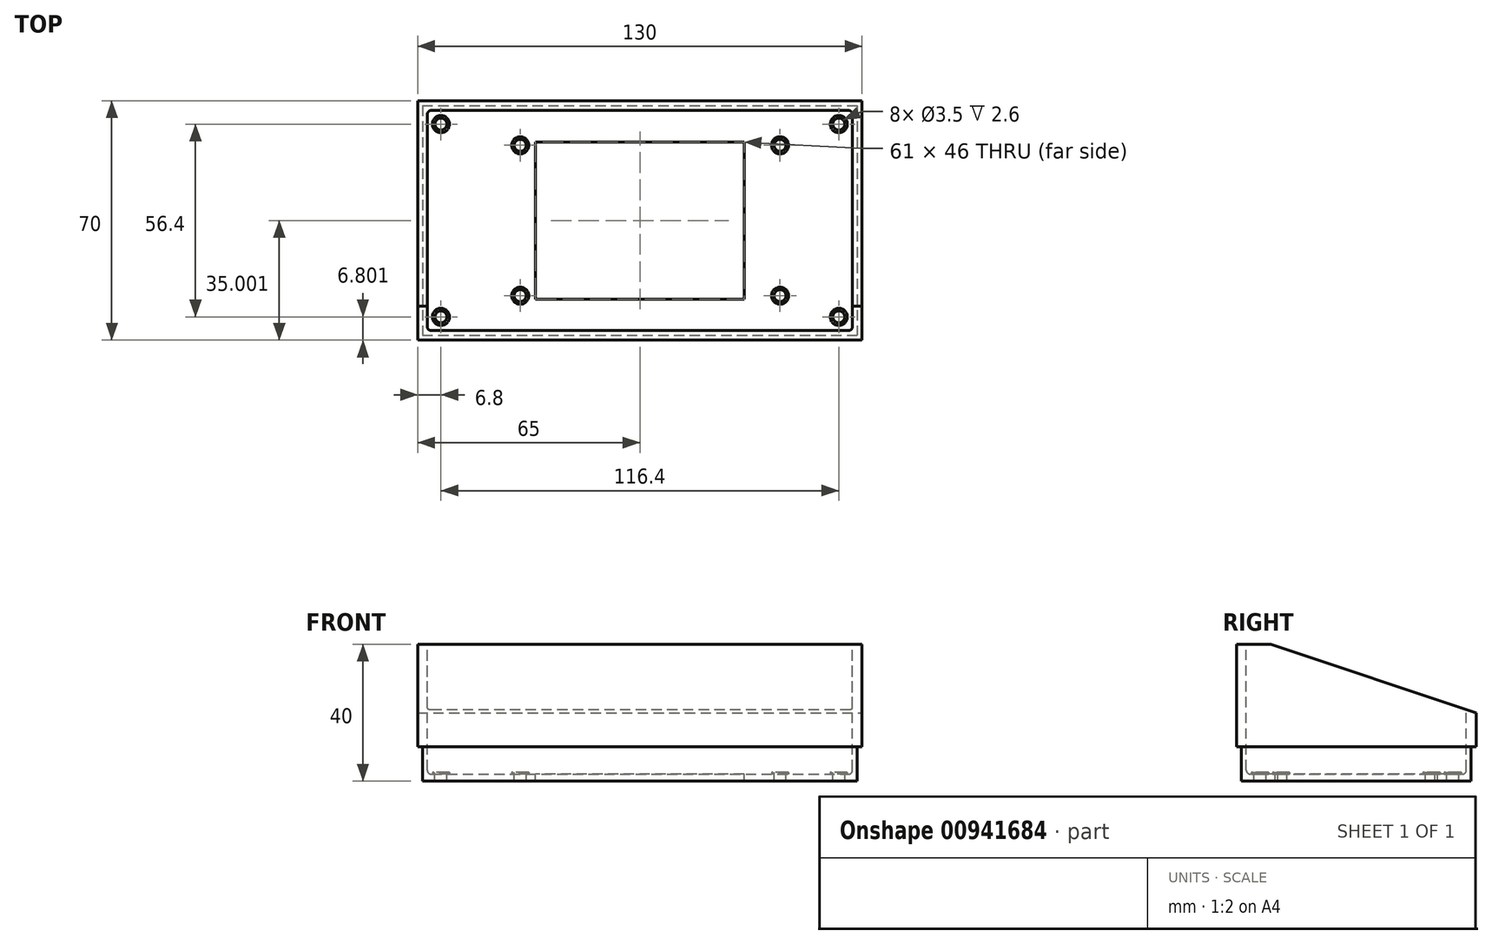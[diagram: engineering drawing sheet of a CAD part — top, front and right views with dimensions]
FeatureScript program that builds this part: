
annotation { "Feature Type Name" : "Feature", "Feature Type Description" : "" }
export const myFeature = defineFeature(function(context is Context, id is Id, definition is map)
    precondition{}
    {
        {
            var Q0;
            Q0=qCreatedBy(makeId("Top.planeOp"),FACE);
            var sketch = newSketch(context, id + "F0", { "sketchPlane" : qUnion([Q0])});
            skLineSegment(sketch, "E0.bottom", {"start": v(-87.5, 48.26) * mm, "end": v(42.5, 48.26) * mm});
            skLineSegment(sketch, "E0.top", {"start": v(-87.5, -21.74) * mm, "end": v(42.5, -21.74) * mm});
            skLineSegment(sketch, "E0.left", {"start": v(-87.5, 48.26) * mm, "end": v(-87.5, -21.74) * mm});
            skLineSegment(sketch, "E0.right", {"start": v(42.5, 48.26) * mm, "end": v(42.5, -21.74) * mm});
            skSolve(sketch);
        }
        {
            var Q0;
            Q0=makeQuery(id+"F0.imprint","IMPRINT",FACE,{"disambiguationData":[TD([[makeQuery(id+"F0.imprint","IMPRINT",EDGE,{"derivedFrom":sQuery(id+"F0.wireOp",EDGE,"E0.bottom")}),-1.0]])]});
            extrude(context, id + "F1", {"entities" : qUnion([Q0]), "depth" : 40 * mm, "offsetDistance" : 25 * mm});
        }
        {
            var Q0;
            Q0=makeQuery(id+"F1.opExtrude","CAP_FACE",FACE,{"disambiguationData":[OSD([sQuery(id+"F0.wireOp",EDGE,"E0.bottom"),sQuery(id+"F0.wireOp",EDGE,"E0.top"),sQuery(id+"F0.wireOp",EDGE,"E0.left"),sQuery(id+"F0.wireOp",EDGE,"E0.right")])],"isStart":false});
            var sketch = newSketch(context, id + "F2", { "sketchPlane" : qUnion([Q0])});
            skLineSegment(sketch, "E1.0", {"start": v(39.7, 45.46) * mm, "end": v(39.7, -18.94) * mm});
            skLineSegment(sketch, "E1.1", {"start": v(-84.7, 45.46) * mm, "end": v(39.7, 45.46) * mm});
            skLineSegment(sketch, "E1.2", {"start": v(-84.7, 45.46) * mm, "end": v(-84.7, -18.94) * mm});
            skLineSegment(sketch, "E1.3", {"start": v(-84.7, -18.94) * mm, "end": v(39.7, -18.94) * mm});
            skSolve(sketch);
        }
        {
            var Q0;
            Q0=makeQuery(id+"F2.imprint","IMPRINT",FACE,{"disambiguationData":[TD([[makeQuery(id+"F2.imprint","IMPRINT",EDGE,{"derivedFrom":sQuery(id+"F2.wireOp",EDGE,"E1.0")}),-1.0]])]});
            extrude(context, id + "F3", {"entities" : qUnion([Q0]), "operationType" : NewBodyOperationType.REMOVE, "oppositeDirection" : true, "depth" : 38 * mm, "offsetDistance" : 25 * mm});
        }
        {
            var Q0;
            Q0=makeQuery(id+"F1.opExtrude","SWEPT_FACE",FACE,{"disambiguationData":[OSD([sQuery(id+"F0.wireOp",EDGE,"E0.right")])]});
            var sketch = newSketch(context, id + "F4", { "sketchPlane" : qUnion([Q0])});
            skLineSegment(sketch, "E2", {"start": v(-11.74, 40) * mm, "end": v(48.26, 20) * mm});
            skLineSegment(sketch, "E3", {"start": v(48.26, 20) * mm, "end": v(48.26, 40) * mm});
            skLineSegment(sketch, "E4", {"start": v(48.26, 40) * mm, "end": v(-11.74, 40) * mm});
            skSolve(sketch);
        }
        {
            var Q0;
            Q0=makeQuery(id+"F4.imprint","IMPRINT",FACE,{"disambiguationData":[TD([[makeQuery(id+"F4.imprint","IMPRINT",EDGE,{"derivedFrom":sQuery(id+"F4.wireOp",EDGE,"E2")}),1.0]])]});
            extrude(context, id + "F5", {"entities" : qUnion([Q0]), "operationType" : NewBodyOperationType.REMOVE, "oppositeDirection" : true, "depth" : 146.2 * mm, "offsetDistance" : 25 * mm});
        }
        {
            var Q0;
            Q0=makeQuery(id+"F1.opExtrude","CAP_FACE",FACE,{"disambiguationData":[OSD([sQuery(id+"F0.wireOp",EDGE,"E0.bottom"),sQuery(id+"F0.wireOp",EDGE,"E0.top"),sQuery(id+"F0.wireOp",EDGE,"E0.left"),sQuery(id+"F0.wireOp",EDGE,"E0.right")])],"isStart":true});
            var sketch = newSketch(context, id + "F6", { "sketchPlane" : qUnion([Q0])});
            skLineSegment(sketch, "E5.0", {"start": v(-86.1, -46.86) * mm, "end": v(41.1, -46.86) * mm});
            skLineSegment(sketch, "E5.1", {"start": v(-86.1, -46.86) * mm, "end": v(-86.1, 20.34) * mm});
            skLineSegment(sketch, "E5.2", {"start": v(-86.1, 20.34) * mm, "end": v(41.1, 20.34) * mm});
            skLineSegment(sketch, "E5.3", {"start": v(41.1, -46.86) * mm, "end": v(41.1, 20.34) * mm});
            skLineSegment(sketch, "E6.bottom", {"start": v(42.5, -48.26) * mm, "end": v(-87.5, -48.26) * mm});
            skLineSegment(sketch, "E6.top", {"start": v(42.5, 21.74) * mm, "end": v(-87.5, 21.74) * mm});
            skLineSegment(sketch, "E6.left", {"start": v(42.5, -48.26) * mm, "end": v(42.5, 21.74) * mm});
            skLineSegment(sketch, "E6.right", {"start": v(-87.5, -48.26) * mm, "end": v(-87.5, 21.74) * mm});
            skSolve(sketch);
        }
        {
            var Q0;
            Q0=makeQuery(id+"F6.imprint","IMPRINT",FACE,{"disambiguationData":[TD([[makeQuery(id+"F6.imprint","IMPRINT",EDGE,{"derivedFrom":sQuery(id+"F6.wireOp",EDGE,"E5.0")}),-1.0]])]});
            extrude(context, id + "F7", {"entities" : qUnion([Q0]), "operationType" : NewBodyOperationType.REMOVE, "oppositeDirection" : true, "depth" : 10 * mm, "offsetDistance" : 25 * mm});
        }
        {
            var Q0;
            Q0=makeQuery(id+"F3.boolean.opBoolean","COPY",FACE,{"derivedFrom":makeQuery(id+"F3.opExtrude","CAP_FACE",FACE,{"disambiguationData":[OSD([sQuery(id+"F2.wireOp",EDGE,"E1.0"),sQuery(id+"F2.wireOp",EDGE,"E1.1"),sQuery(id+"F2.wireOp",EDGE,"E1.2"),sQuery(id+"F2.wireOp",EDGE,"E1.3")])],"isStart":false})});
            var sketch = newSketch(context, id + "F8", { "sketchPlane" : qUnion([Q0])});
            skLineSegment(sketch, "E7.bottom", {"start": v(8, -9.74) * mm, "end": v(-53, -9.74) * mm});
            skLineSegment(sketch, "E7.top", {"start": v(8, 36.26) * mm, "end": v(-53, 36.26) * mm});
            skLineSegment(sketch, "E7.left", {"start": v(8, -9.74) * mm, "end": v(8, 36.26) * mm});
            skLineSegment(sketch, "E7.right", {"start": v(-53, -9.74) * mm, "end": v(-53, 36.26) * mm});
            skLineSegment(sketch, "E8.0", {"start": v(-57.5, -9.74) * mm, "end": v(-57.5, 36.26) * mm, "construction": true});
            skLineSegment(sketch, "E9.0", {"start": v(18.5, -9.74) * mm, "end": v(18.5, 36.26) * mm, "construction": true});
            skLineSegment(sketch, "E10.0", {"start": v(18.5, -8.74) * mm, "end": v(-57.5, -8.74) * mm, "construction": true});
            skLineSegment(sketch, "E11.0", {"start": v(18.5, 35.26) * mm, "end": v(-57.5, 35.26) * mm, "construction": true});
            skCircle(sketch, "E12", {"center": v(18.5, -8.74) * mm, "radius": 1.75 * mm});
            skCircle(sketch, "E13", {"center": v(18.5, 35.26) * mm, "radius": 1.75 * mm});
            skCircle(sketch, "E14", {"center": v(-57.5, -8.74) * mm, "radius": 1.75 * mm});
            skCircle(sketch, "E15", {"center": v(-57.5, 35.26) * mm, "radius": 1.75 * mm});
            skSolve(sketch);
        }
        {
            var Q0;
            Q0=makeQuery(id+"F8.imprint","IMPRINT",FACE,{"disambiguationData":[TD([[makeQuery(id+"F8.imprint","IMPRINT",EDGE,{"derivedFrom":sQuery(id+"F8.wireOp",EDGE,"E7.bottom")}),-1.0]])]});
            var Q1;
            Q1=makeQuery(id+"F8.imprint","IMPRINT",FACE,{"disambiguationData":[TD([[makeQuery(id+"F8.imprint","IMPRINT",EDGE,{"derivedFrom":sQuery(id+"F8.wireOp",EDGE,"E15")}),1.0]])]});
            var Q2;
            Q2=makeQuery(id+"F8.imprint","IMPRINT",FACE,{"disambiguationData":[TD([[makeQuery(id+"F8.imprint","IMPRINT",EDGE,{"derivedFrom":sQuery(id+"F8.wireOp",EDGE,"E13")}),1.0]])]});
            var Q3;
            Q3=makeQuery(id+"F8.imprint","IMPRINT",FACE,{"disambiguationData":[TD([[makeQuery(id+"F8.imprint","IMPRINT",EDGE,{"derivedFrom":sQuery(id+"F8.wireOp",EDGE,"E12")}),1.0]])]});
            var Q4;
            Q4=makeQuery(id+"F8.imprint","IMPRINT",FACE,{"disambiguationData":[TD([[makeQuery(id+"F8.imprint","IMPRINT",EDGE,{"derivedFrom":sQuery(id+"F8.wireOp",EDGE,"E14")}),1.0]])]});
            extrude(context, id + "F9", {"entities" : qUnion([Q0, Q1, Q2, Q3, Q4]), "operationType" : NewBodyOperationType.REMOVE, "oppositeDirection" : true, "depth" : 25 * mm, "offsetDistance" : 25 * mm, "hasSecondDirection" : true, "secondDirectionOppositeDirection" : false, "secondDirectionDepth" : 25 * mm});
        }
        {
            var Q0;
            Q0=makeQuery(id+"F3.boolean.opBoolean","COPY",FACE,{"derivedFrom":makeQuery(id+"F3.opExtrude","CAP_FACE",FACE,{"disambiguationData":[OSD([sQuery(id+"F2.wireOp",EDGE,"E1.0"),sQuery(id+"F2.wireOp",EDGE,"E1.1"),sQuery(id+"F2.wireOp",EDGE,"E1.2"),sQuery(id+"F2.wireOp",EDGE,"E1.3")])],"isStart":false})});
            var sketch = newSketch(context, id + "F10", { "sketchPlane" : qUnion([Q0])});
            skCircle(sketch, "E16", {"center": v(-80.7, 41.46) * mm, "radius": 1.75 * mm});
            skCircle(sketch, "E17", {"center": v(-80.7, -14.94) * mm, "radius": 1.75 * mm});
            skCircle(sketch, "E18", {"center": v(35.7, -14.94) * mm, "radius": 1.75 * mm});
            skCircle(sketch, "E19", {"center": v(35.7, 41.46) * mm, "radius": 1.75 * mm});
            skSolve(sketch);
        }
        {
            var Q0;
            Q0=makeQuery(id+"F10.imprint","IMPRINT",FACE,{"disambiguationData":[TD([[makeQuery(id+"F10.imprint","IMPRINT",EDGE,{"derivedFrom":sQuery(id+"F10.wireOp",EDGE,"E16")}),1.0]])]});
            var Q1;
            Q1=makeQuery(id+"F10.imprint","IMPRINT",FACE,{"disambiguationData":[TD([[makeQuery(id+"F10.imprint","IMPRINT",EDGE,{"derivedFrom":sQuery(id+"F10.wireOp",EDGE,"E19")}),1.0]])]});
            var Q2;
            Q2=makeQuery(id+"F10.imprint","IMPRINT",FACE,{"disambiguationData":[TD([[makeQuery(id+"F10.imprint","IMPRINT",EDGE,{"derivedFrom":sQuery(id+"F10.wireOp",EDGE,"E18")}),1.0]])]});
            var Q3;
            Q3=makeQuery(id+"F10.imprint","IMPRINT",FACE,{"disambiguationData":[TD([[makeQuery(id+"F10.imprint","IMPRINT",EDGE,{"derivedFrom":sQuery(id+"F10.wireOp",EDGE,"E17")}),1.0]])]});
            extrude(context, id + "F11", {"entities" : qUnion([Q0, Q1, Q2, Q3]), "operationType" : NewBodyOperationType.REMOVE, "oppositeDirection" : true, "depth" : 25 * mm, "offsetDistance" : 25 * mm});
        }
        {
            var Q0;
            Q0=makeQuery(id+"F3.boolean.opBoolean","COPY",FACE,{"derivedFrom":makeQuery(id+"F3.opExtrude","CAP_FACE",FACE,{"disambiguationData":[OSD([sQuery(id+"F2.wireOp",EDGE,"E1.0"),sQuery(id+"F2.wireOp",EDGE,"E1.1"),sQuery(id+"F2.wireOp",EDGE,"E1.2"),sQuery(id+"F2.wireOp",EDGE,"E1.3")])],"isStart":false})});
            var sketch = newSketch(context, id + "F12", { "sketchPlane" : qUnion([Q0])});
            skCircle(sketch, "E20", {"center": v(-57.5, 35.26) * mm, "radius": 2.5 * mm});
            skCircle(sketch, "E21", {"center": v(18.5, 35.26) * mm, "radius": 2.5 * mm});
            skCircle(sketch, "E22", {"center": v(18.5, -8.74) * mm, "radius": 2.5 * mm});
            skCircle(sketch, "E23", {"center": v(-57.5, -8.74) * mm, "radius": 2.5 * mm});
            skCircle(sketch, "E24", {"center": v(-80.7, -14.94) * mm, "radius": 2.5 * mm});
            skCircle(sketch, "E25", {"center": v(-80.7, 41.46) * mm, "radius": 2.5 * mm});
            skCircle(sketch, "E26", {"center": v(35.7, 41.46) * mm, "radius": 2.5 * mm});
            skCircle(sketch, "E27", {"center": v(-80.7, 41.46) * mm, "radius": 1.75 * mm});
            skCircle(sketch, "E28", {"center": v(-57.5, 35.26) * mm, "radius": 1.75 * mm});
            skCircle(sketch, "E29", {"center": v(18.5, 35.26) * mm, "radius": 1.75 * mm});
            skCircle(sketch, "E30", {"center": v(35.7, 41.46) * mm, "radius": 1.75 * mm});
            skCircle(sketch, "E31", {"center": v(18.5, -8.74) * mm, "radius": 1.75 * mm});
            skCircle(sketch, "E32", {"center": v(35.7, -14.94) * mm, "radius": 1.75 * mm});
            skCircle(sketch, "E33", {"center": v(35.7, -14.94) * mm, "radius": 2.5 * mm});
            skCircle(sketch, "E34", {"center": v(-57.5, -8.74) * mm, "radius": 1.75 * mm});
            skCircle(sketch, "E35", {"center": v(-80.7, -14.94) * mm, "radius": 1.75 * mm});
            skSolve(sketch);
        }
        {
            var Q0;
            Q0 = qSketchRegion(id + "F12", true);
            extrude(context, id + "F13", {"entities" : qUnion([Q0]), "operationType" : NewBodyOperationType.ADD, "depth" : .6 * mm, "offsetDistance" : 25 * mm});
        }
        {
            var Q0;
            Q0=makeQuery(id+"F3.boolean.opBoolean","COPY",EDGE,{"derivedFrom":makeQuery(id+"F3.opExtrude","SWEPT_EDGE",EDGE,{"disambiguationData":[OSD([sQuery(id+"F2.wireOp",EDGE,"E1.0"),sQuery(id+"F2.wireOp",EDGE,"E1.1")])]})});
            var Q1;
            Q1=makeQuery(id+"F3.boolean.opBoolean","COPY",EDGE,{"derivedFrom":makeQuery(id+"F3.opExtrude","SWEPT_EDGE",EDGE,{"disambiguationData":[OSD([sQuery(id+"F2.wireOp",EDGE,"E1.1"),sQuery(id+"F2.wireOp",EDGE,"E1.2")])]})});
            var Q2;
            Q2=makeQuery(id+"F3.boolean.opBoolean","COPY",EDGE,{"derivedFrom":makeQuery(id+"F3.opExtrude","SWEPT_EDGE",EDGE,{"disambiguationData":[OSD([sQuery(id+"F2.wireOp",EDGE,"E1.2"),sQuery(id+"F2.wireOp",EDGE,"E1.3")])]})});
            var Q3;
            Q3=makeQuery(id+"F3.boolean.opBoolean","COPY",EDGE,{"derivedFrom":makeQuery(id+"F3.opExtrude","SWEPT_EDGE",EDGE,{"disambiguationData":[OSD([sQuery(id+"F2.wireOp",EDGE,"E1.0"),sQuery(id+"F2.wireOp",EDGE,"E1.3")])]})});
            var Q4;
            Q4=makeQuery(id+"F3.boolean.opBoolean","COPY",EDGE,{"derivedFrom":makeQuery(id+"F3.opExtrude","CAP_EDGE",EDGE,{"disambiguationData":[OSD([sQuery(id+"F2.wireOp",EDGE,"E1.2")])],"isStart":false})});
            var Q5;
            Q5=makeQuery(id+"F3.boolean.opBoolean","COPY",EDGE,{"derivedFrom":makeQuery(id+"F3.opExtrude","CAP_EDGE",EDGE,{"disambiguationData":[OSD([sQuery(id+"F2.wireOp",EDGE,"E1.3")])],"isStart":false})});
            var Q6;
            Q6=makeQuery(id+"F3.boolean.opBoolean","COPY",EDGE,{"derivedFrom":makeQuery(id+"F3.opExtrude","CAP_EDGE",EDGE,{"disambiguationData":[OSD([sQuery(id+"F2.wireOp",EDGE,"E1.0")])],"isStart":false})});
            var Q7;
            Q7=makeQuery(id+"F3.boolean.opBoolean","COPY",EDGE,{"derivedFrom":makeQuery(id+"F3.opExtrude","CAP_EDGE",EDGE,{"disambiguationData":[OSD([sQuery(id+"F2.wireOp",EDGE,"E1.1")])],"isStart":false})});
            fillet(context, id + "F14", {"entities" : qUnion([Q0, Q1, Q2, Q3, Q4, Q5, Q6, Q7]), "radius" : 1.2 * mm, "tangentPropagation" : true, "allowEdgeOverflow" : false});
        }
    });
